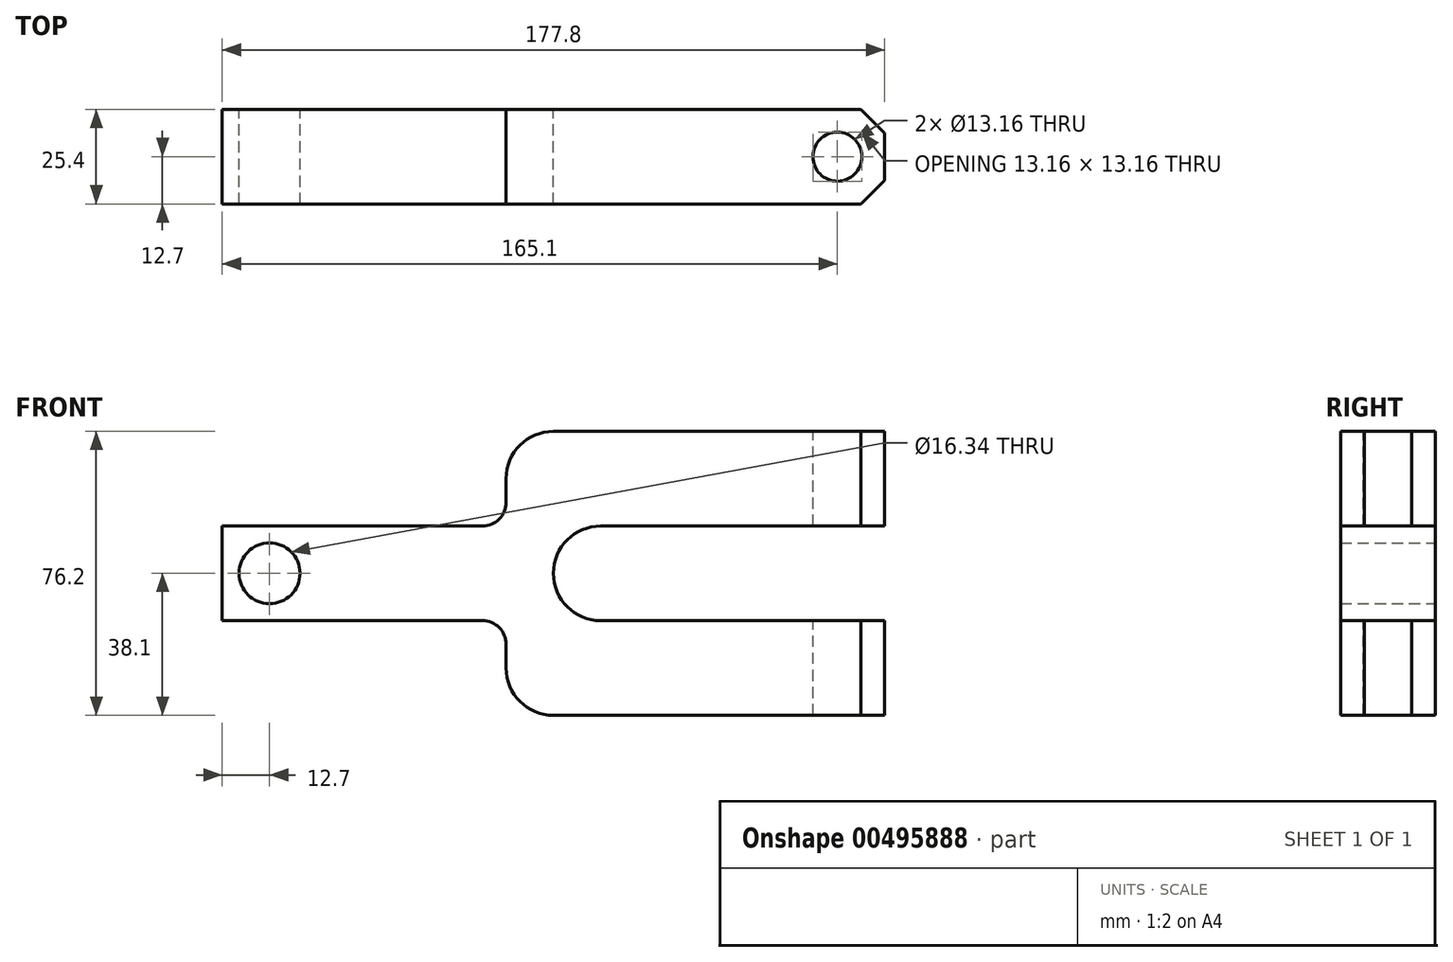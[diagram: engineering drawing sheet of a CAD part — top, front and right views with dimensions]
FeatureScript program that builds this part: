
annotation { "Feature Type Name" : "Feature", "Feature Type Description" : "" }
export const myFeature = defineFeature(function(context is Context, id is Id, definition is map)
    precondition{}
    {
        {
            var Q0;
            Q0=qCreatedBy(makeId("Front.planeOp"),FACE);
            var sketch = newSketch(context, id + "F0", { "sketchPlane" : qUnion([Q0])});
            skLineSegment(sketch, "E0", {"start": v(0, 0) * mm, "end": v(0, 25.4) * mm});
            skLineSegment(sketch, "E1", {"start": v(0, 25.4) * mm, "end": v(76.2, 25.4) * mm});
            skLineSegment(sketch, "E2", {"start": v(0, 0) * mm, "end": v(76.2, 0) * mm});
            skLineSegment(sketch, "E3", {"start": v(76.2, 25.4) * mm, "end": v(76.2, 38.1) * mm});
            skLineSegment(sketch, "E4", {"start": v(76.2, 0) * mm, "end": v(76.2, -12.7) * mm});
            skLineSegment(sketch, "E5", {"start": v(88.9, -25.4) * mm, "end": v(177.8, -25.4) * mm});
            skLineSegment(sketch, "E6", {"start": v(177.8, -25.4) * mm, "end": v(177.8, 0) * mm});
            skLineSegment(sketch, "E7", {"start": v(177.8, 0) * mm, "end": v(101.6, 0) * mm});
            skLineSegment(sketch, "E8", {"start": v(88.9, 12.7) * mm, "end": v(88.9, 12.7) * mm});
            skLineSegment(sketch, "E9", {"start": v(101.6, 25.4) * mm, "end": v(177.8, 25.4) * mm});
            skLineSegment(sketch, "E10", {"start": v(177.8, 25.4) * mm, "end": v(177.8, 50.8) * mm});
            skLineSegment(sketch, "E11", {"start": v(177.8, 50.8) * mm, "end": v(88.9, 50.8) * mm});
            skPoint(sketch, "E12.visualSharp", {"position": v(76.2, 50.8) * mm});
            skArc(sketch, "E12.filletArc", {"start": v(88.9, 50.8) * mm, "mid": v(79.92, 47.08) * mm, "end": v(76.2, 38.1) * mm});
            skPoint(sketch, "E13.visualSharp", {"position": v(88.9, 25.4) * mm});
            skArc(sketch, "E13.filletArc", {"start": v(101.6, 25.4) * mm, "mid": v(92.62, 21.68) * mm, "end": v(88.9, 12.7) * mm});
            skPoint(sketch, "E14.visualSharp", {"position": v(88.9, 0) * mm});
            skArc(sketch, "E14.filletArc", {"start": v(88.9, 12.7) * mm, "mid": v(92.62, 3.72) * mm, "end": v(101.6, 0) * mm});
            skPoint(sketch, "E15.visualSharp", {"position": v(76.2, -25.4) * mm});
            skArc(sketch, "E15.filletArc", {"start": v(76.2, -12.7) * mm, "mid": v(79.92, -21.68) * mm, "end": v(88.9, -25.4) * mm});
            skCircle(sketch, "E16", {"center": v(12.7, 12.7) * mm, "radius": 8.17 * mm});
            skSolve(sketch);
        }
        {
            var Q0;
            Q0 = qSketchRegion(id + "F0", true);
            extrude(context, id + "F1", {"entities" : qUnion([Q0]), "endBound" : BoundingType.SYMMETRIC, "depth" : 25.4 * mm});
        }
        {
            var Q0;
            Q0=makeQuery(id+"F1.opExtrude","SWEPT_FACE",FACE,{"disambiguationData":[OSD([sQuery(id+"F0.wireOp",EDGE,"E11")])]});
            var sketch = newSketch(context, id + "F2", { "sketchPlane" : qUnion([Q0])});
            skCircle(sketch, "E17", {"center": v(165.1, 0) * mm, "radius": 6.62 * mm});
            skCircle(sketch, "E18", {"center": v(165.1, 0) * mm, "radius": 6.6 * mm});
            skCircle(sketch, "E19", {"center": v(165.1, 0) * mm, "radius": 6.58 * mm});
            skSolve(sketch);
        }
        {
            var Q0;
            Q0=makeQuery(id+"F2.imprint","IMPRINT",FACE,{"disambiguationData":[TD([[makeQuery(id+"F2.imprint","IMPRINT",EDGE,{"derivedFrom":sQuery(id+"F2.wireOp",EDGE,"E19")}),1.0]])]});
            extrude(context, id + "F3", {"entities" : qUnion([Q0]), "operationType" : NewBodyOperationType.REMOVE, "endBound" : BoundingType.SYMMETRIC, "oppositeDirection" : true, "depth" : 254 * mm});
        }
        {
            var Q0;
            Q0=makeQuery(id+"F1.opExtrude","SWEPT_EDGE",EDGE,{"disambiguationData":[OSD([sQuery(id+"F0.wireOp",EDGE,"E1"),sQuery(id+"F0.wireOp",EDGE,"E3")])]});
            var Q1;
            Q1=makeQuery(id+"F1.opExtrude","SWEPT_EDGE",EDGE,{"disambiguationData":[OSD([sQuery(id+"F0.wireOp",EDGE,"E2"),sQuery(id+"F0.wireOp",EDGE,"E4")])]});
            fillet(context, id + "F4", {"entities" : qUnion([Q0, Q1]), "radius" : 6.35 * mm, "tangentPropagation" : true, "allowEdgeOverflow" : false});
        }
        {
            var Q0;
            Q0=makeQuery(id+"F1.opExtrude","CAP_EDGE",EDGE,{"disambiguationData":[OSD([sQuery(id+"F0.wireOp",EDGE,"E10")])],"isStart":true});
            var Q1;
            Q1=makeQuery(id+"F1.opExtrude","CAP_EDGE",EDGE,{"disambiguationData":[OSD([sQuery(id+"F0.wireOp",EDGE,"E10")])],"isStart":false});
            var Q2;
            Q2=makeQuery(id+"F1.opExtrude","CAP_EDGE",EDGE,{"disambiguationData":[OSD([sQuery(id+"F0.wireOp",EDGE,"E6")])],"isStart":false});
            var Q3;
            Q3=makeQuery(id+"F1.opExtrude","CAP_EDGE",EDGE,{"disambiguationData":[OSD([sQuery(id+"F0.wireOp",EDGE,"E6")])],"isStart":true});
            chamfer(context, id + "F5", {"entities" : qUnion([Q0, Q1, Q2, Q3]), "width" : 6.35 * mm, "tangentPropagation" : true});
        }
    });
